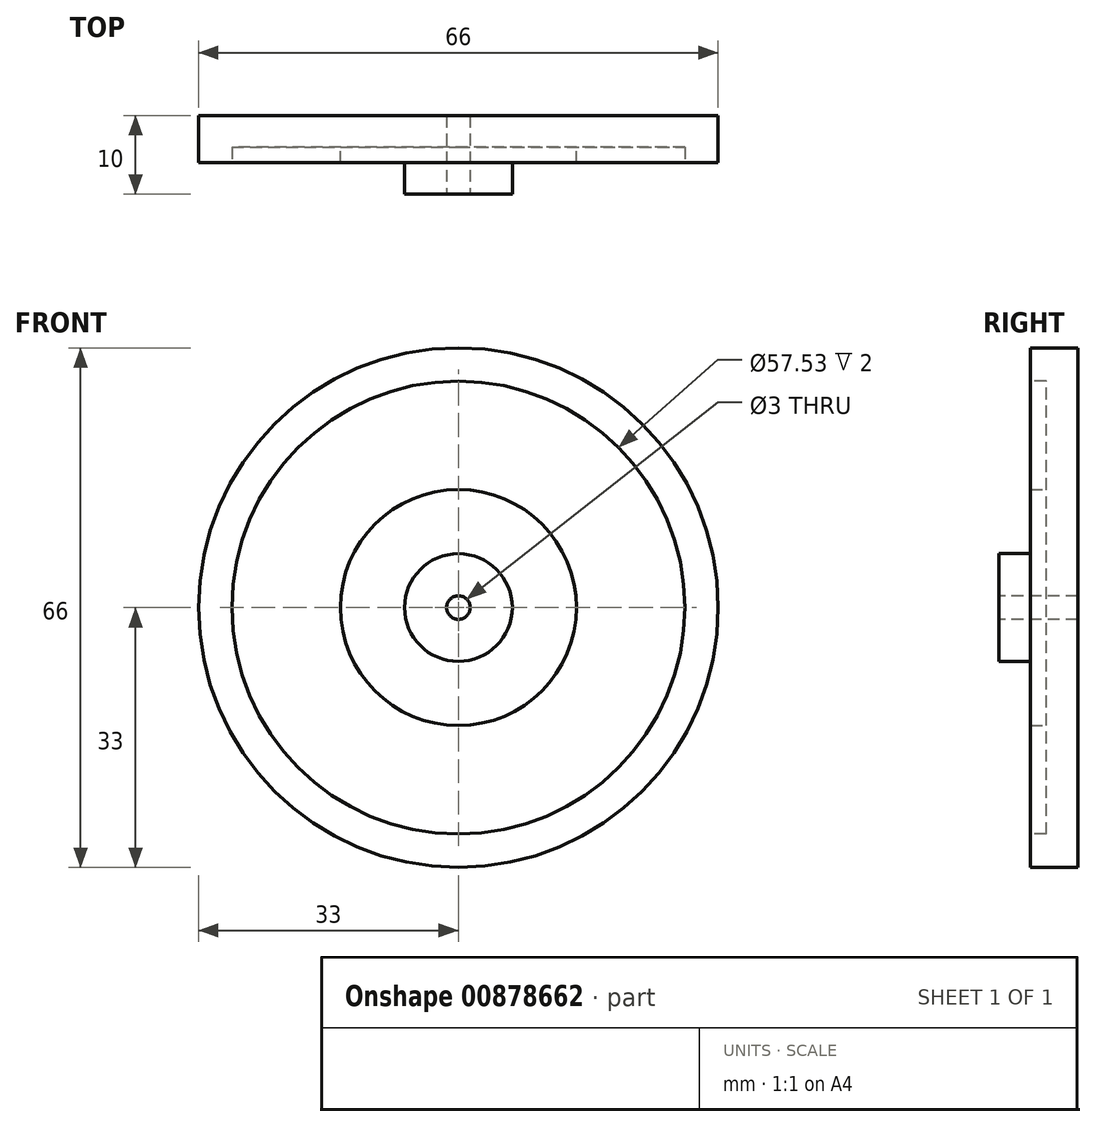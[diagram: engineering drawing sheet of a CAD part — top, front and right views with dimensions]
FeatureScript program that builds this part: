
annotation { "Feature Type Name" : "Feature", "Feature Type Description" : "" }
export const myFeature = defineFeature(function(context is Context, id is Id, definition is map)
    precondition{}
    {
        {
            var Q0;
            Q0=qCreatedBy(makeId("Front.planeOp"),FACE);
            var sketch = newSketch(context, id + "F0", { "sketchPlane" : qUnion([Q0])});
            skCircle(sketch, "E0", {"center": v(0, 0) * mm, "radius": 33 * mm});
            skSolve(sketch);
        }
        {
            var Q0;
            Q0 = qSketchRegion(id + "F0", true);
            var Q1;
            Q1=makeQuery(id+"F0.imprint","IMPRINT",FACE,{"disambiguationData":[TD([[makeQuery(id+"F0.imprint","IMPRINT",EDGE,{"derivedFrom":sQuery(id+"F0.wireOp",EDGE,"E0")}),1.0]])]});
            extrude(context, id + "F1", {"entities" : qUnion([Q0, Q1]), "depth" : 6 * mm, "offsetDistance" : 25 * mm});
        }
        {
            var Q0;
            Q0=makeQuery(id+"F1.opExtrude","CAP_FACE",FACE,{"disambiguationData":[OSD([sQuery(id+"F0.wireOp",EDGE,"E0")])],"isStart":false});
            var sketch = newSketch(context, id + "F2", { "sketchPlane" : qUnion([Q0])});
            skCircle(sketch, "E1", {"center": v(0, 0) * mm, "radius": 28.76 * mm});
            skSolve(sketch);
        }
        {
            var Q0;
            Q0 = qSketchRegion(id + "F2", true);
            extrude(context, id + "F3", {"entities" : qUnion([Q0]), "operationType" : NewBodyOperationType.REMOVE, "oppositeDirection" : true, "depth" : 2 * mm, "offsetDistance" : 25 * mm});
        }
        {
            var Q0;
            Q0=makeQuery(id+"F3.boolean.opBoolean","COPY",FACE,{"derivedFrom":makeQuery(id+"F3.opExtrude","CAP_FACE",FACE,{"disambiguationData":[OSD([sQuery(id+"F2.wireOp",EDGE,"E1")])],"isStart":false})});
            var sketch = newSketch(context, id + "F4", { "sketchPlane" : qUnion([Q0])});
            skCircle(sketch, "E2", {"center": v(0, 0) * mm, "radius": 14.99 * mm});
            skSolve(sketch);
        }
        {
            var Q0;
            Q0 = qSketchRegion(id + "F4", true);
            extrude(context, id + "F5", {"entities" : qUnion([Q0]), "operationType" : NewBodyOperationType.ADD, "depth" : 2 * mm, "offsetDistance" : 25 * mm});
        }
        {
            var Q0;
            Q0=makeQuery(id+"F5.opExtrude","CAP_FACE",FACE,{"disambiguationData":[OSD([sQuery(id+"F4.wireOp",EDGE,"E2")])],"isStart":false});
            var sketch = newSketch(context, id + "F6", { "sketchPlane" : qUnion([Q0])});
            skCircle(sketch, "E3", {"center": v(0, 0) * mm, "radius": 6.84 * mm});
            skSolve(sketch);
        }
        {
            var Q0;
            Q0=makeQuery(id+"F6.imprint","IMPRINT",FACE,{"disambiguationData":[TD([[makeQuery(id+"F6.imprint","IMPRINT",EDGE,{"derivedFrom":sQuery(id+"F6.wireOp",EDGE,"E3")}),1.0]])]});
            extrude(context, id + "F7", {"entities" : qUnion([Q0]), "operationType" : NewBodyOperationType.ADD, "depth" : 4 * mm, "offsetDistance" : 25 * mm});
        }
        {
            var Q0;
            Q0=makeQuery(id+"F7.opExtrude","CAP_FACE",FACE,{"disambiguationData":[OSD([sQuery(id+"F6.wireOp",EDGE,"E3")])],"isStart":false});
            var sketch = newSketch(context, id + "F8", { "sketchPlane" : qUnion([Q0])});
            skCircle(sketch, "E4", {"center": v(0, 0) * mm, "radius": 1.5 * mm});
            skSolve(sketch);
        }
        {
            var Q0;
            Q0=makeQuery(id+"F8.imprint","IMPRINT",FACE,{"disambiguationData":[TD([[makeQuery(id+"F8.imprint","IMPRINT",EDGE,{"derivedFrom":sQuery(id+"F8.wireOp",EDGE,"E4")}),1.0]])]});
            extrude(context, id + "F9", {"entities" : qUnion([Q0]), "operationType" : NewBodyOperationType.REMOVE, "oppositeDirection" : true, "depth" : 25 * mm, "offsetDistance" : 25 * mm});
        }
    });
